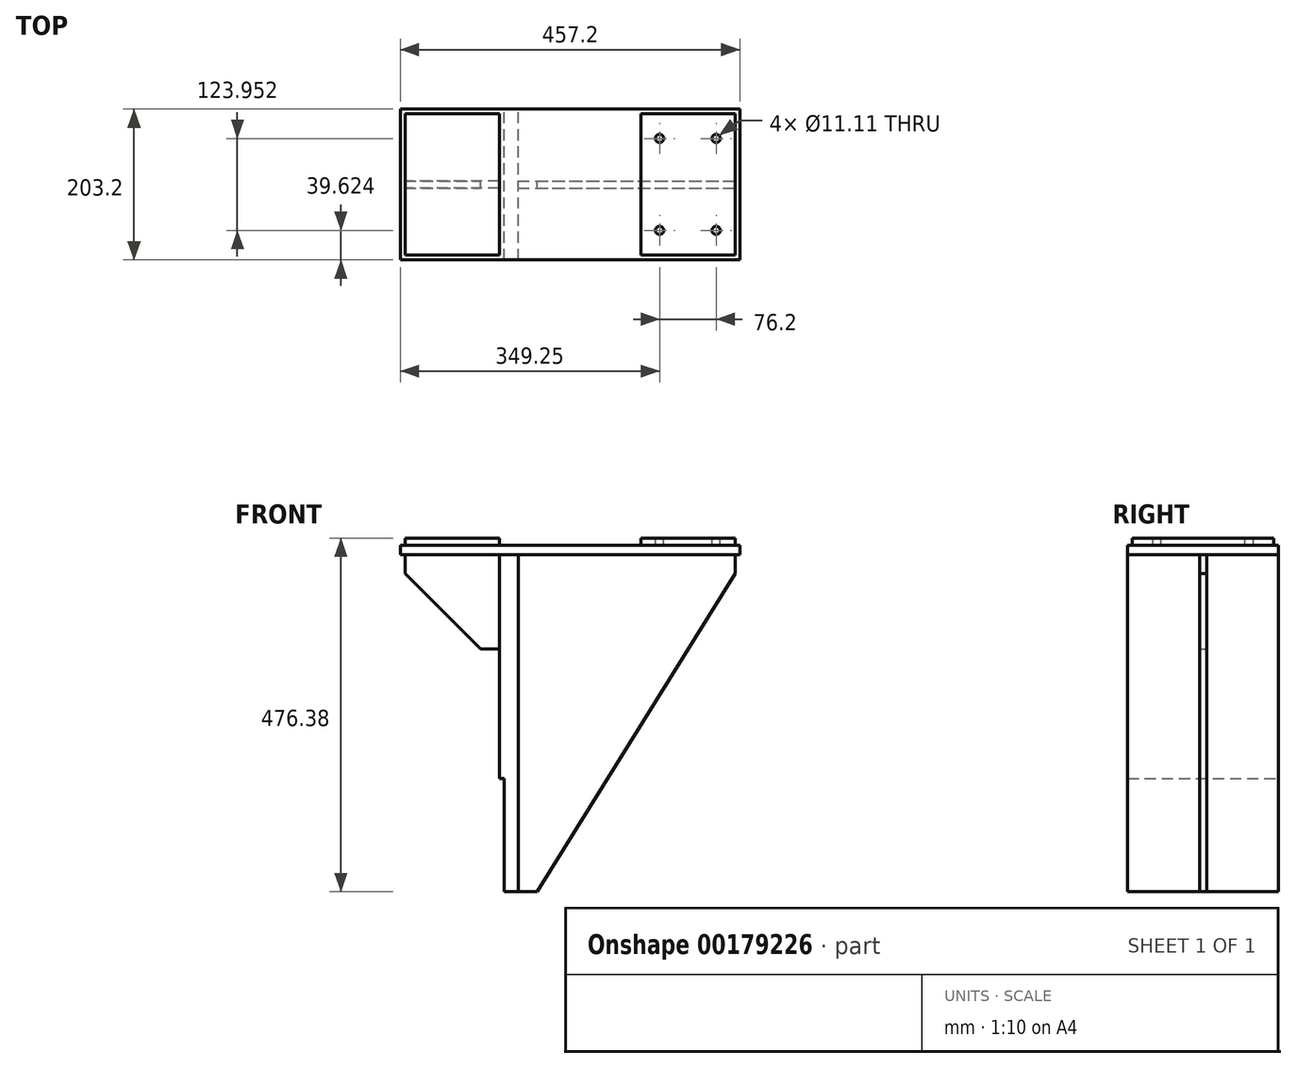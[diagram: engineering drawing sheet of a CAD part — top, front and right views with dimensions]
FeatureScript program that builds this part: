
annotation { "Feature Type Name" : "Feature", "Feature Type Description" : "" }
export const myFeature = defineFeature(function(context is Context, id is Id, definition is map)
    precondition{}
    {
        {
            var Q0;
            Q0=qCreatedBy(makeId("Front.planeOp"),FACE);
            var sketch = newSketch(context, id + "F0", { "sketchPlane" : qUnion([Q0])});
            skLineSegment(sketch, "E0.bottom", {"start": v(0, -454.15) * mm, "end": v(-19.05, -454.15) * mm});
            skLineSegment(sketch, "E0.top", {"start": v(0, 0) * mm, "end": v(-19.05, 0) * mm});
            skLineSegment(sketch, "E0.left", {"start": v(0, -454.15) * mm, "end": v(0, 0) * mm});
            skLineSegment(sketch, "E0.right", {"start": v(-19.05, -454.15) * mm, "end": v(-19.05, 0) * mm});
            skLineSegment(sketch, "E1.bottom", {"start": v(-19.05, -301.75) * mm, "end": v(-25.4, -301.75) * mm});
            skLineSegment(sketch, "E1.top", {"start": v(-19.05, 0) * mm, "end": v(-25.4, 0) * mm});
            skLineSegment(sketch, "E1.left", {"start": v(-19.05, -301.75) * mm, "end": v(-19.05, 0) * mm});
            skLineSegment(sketch, "E1.right", {"start": v(-25.4, -301.75) * mm, "end": v(-25.4, 0) * mm});
            skSolve(sketch);
        }
        {
            var Q0;
            Q0=makeQuery(id+"F0.imprint","IMPRINT",FACE,{"disambiguationData":[TD([[makeQuery(id+"F0.imprint","IMPRINT",EDGE,{"derivedFrom":sQuery(id+"F0.wireOp",EDGE,"E0.bottom")}),-1.0]])]});
            var Q1;
            Q1=makeQuery(id+"F0.imprint","IMPRINT",FACE,{"disambiguationData":[TD([[makeQuery(id+"F0.imprint","IMPRINT",EDGE,{"derivedFrom":sQuery(id+"F0.wireOp",EDGE,"E1.bottom")}),-1.0]])]});
            extrude(context, id + "F1", {"entities" : qUnion([Q0, Q1]), "endBound" : BoundingType.SYMMETRIC, "depth" : 203.2 * mm});
        }
        {
            var Q0;
            Q0=qCreatedBy(makeId("Front.planeOp"),FACE);
            var sketch = newSketch(context, id + "F2", { "sketchPlane" : qUnion([Q0])});
            skLineSegment(sketch, "E2", {"start": v(0, 0) * mm, "end": v(-158.75, 0) * mm});
            skLineSegment(sketch, "E3", {"start": v(-158.75, 0) * mm, "end": v(-158.75, 12.7) * mm});
            skLineSegment(sketch, "E4", {"start": v(-158.75, 12.7) * mm, "end": v(298.45, 12.7) * mm});
            skLineSegment(sketch, "E5", {"start": v(298.45, 12.7) * mm, "end": v(298.45, 0) * mm});
            skLineSegment(sketch, "E6", {"start": v(298.45, 0) * mm, "end": v(0, 0) * mm});
            skSolve(sketch);
        }
        {
            var Q0;
            Q0=makeQuery(id+"F2.imprint","IMPRINT",FACE,{"disambiguationData":[TD([[makeQuery(id+"F2.imprint","IMPRINT",EDGE,{"derivedFrom":sQuery(id+"F2.wireOp",EDGE,"E2")}),-1.0]])]});
            extrude(context, id + "F3", {"entities" : qUnion([Q0]), "endBound" : BoundingType.SYMMETRIC, "depth" : 203.2 * mm});
        }
        {
            var Q0;
            Q0=qCreatedBy(makeId("Front.planeOp"),FACE);
            var sketch = newSketch(context, id + "F4", { "sketchPlane" : qUnion([Q0])});
            skLineSegment(sketch, "E7.0", {"start": v(-25.4, -301.75) * mm, "end": v(-25.4, 0) * mm, "construction": true});
            skLineSegment(sketch, "E8.0", {"start": v(298.45, 0) * mm, "end": v(-158.75, 0) * mm, "construction": true});
            skLineSegment(sketch, "E9.0", {"start": v(0, -454.15) * mm, "end": v(0, 0) * mm, "construction": true});
            skLineSegment(sketch, "E10.bottom", {"start": v(-25.4, 0) * mm, "end": v(-152.4, 0) * mm});
            skLineSegment(sketch, "E10.top", {"start": v(-25.4, -127) * mm, "end": v(-50.8, -127) * mm});
            skLineSegment(sketch, "E10.left", {"start": v(-25.4, 0) * mm, "end": v(-25.4, -127) * mm});
            skLineSegment(sketch, "E10.right", {"start": v(-152.4, 0) * mm, "end": v(-152.4, -25.4) * mm});
            skLineSegment(sketch, "E11", {"start": v(-152.4, -25.4) * mm, "end": v(-50.8, -127) * mm});
            skSolve(sketch);
        }
        {
            var Q0;
            Q0 = qSketchRegion(id + "F4", true);
            extrude(context, id + "F5", {"entities" : qUnion([Q0]), "endBound" : BoundingType.SYMMETRIC, "depth" : 9.52 * mm});
        }
        {
            var Q0;
            Q0=qCreatedBy(makeId("Front.planeOp"),FACE);
            var sketch = newSketch(context, id + "F6", { "sketchPlane" : qUnion([Q0])});
            skLineSegment(sketch, "E12.0", {"start": v(298.45, 0) * mm, "end": v(-158.75, 0) * mm, "construction": true});
            skLineSegment(sketch, "E13.0", {"start": v(0, -454.15) * mm, "end": v(0, 0) * mm, "construction": true});
            skLineSegment(sketch, "E14.bottom", {"start": v(0, 0) * mm, "end": v(292.1, 0) * mm});
            skLineSegment(sketch, "E14.top", {"start": v(0, -454.15) * mm, "end": v(25.4, -454.15) * mm});
            skLineSegment(sketch, "E14.left", {"start": v(0, 0) * mm, "end": v(0, -454.15) * mm});
            skLineSegment(sketch, "E14.right", {"start": v(292.1, 0) * mm, "end": v(292.1, -25.4) * mm});
            skLineSegment(sketch, "E15", {"start": v(25.4, -454.15) * mm, "end": v(292.1, -25.4) * mm});
            skPoint(sketch, "E16.orphan", {"position": v(292.1, -454.15) * mm});
            skSolve(sketch);
        }
        {
            var Q0;
            Q0 = qSketchRegion(id + "F6", true);
            extrude(context, id + "F7", {"entities" : qUnion([Q0]), "endBound" : BoundingType.SYMMETRIC, "depth" : 9.52 * mm});
        }
        {
            var Q0;
            Q0=makeQuery(id+"F3.opExtrude","SWEPT_FACE",FACE,{"disambiguationData":[OSD([sQuery(id+"F2.wireOp",EDGE,"E4")])]});
            var sketch = newSketch(context, id + "F8", { "sketchPlane" : qUnion([Q0])});
            skLineSegment(sketch, "E17.0.0", {"start": v(298.45, 101.6) * mm, "end": v(-158.75, 101.6) * mm, "construction": true});
            skLineSegment(sketch, "E17.0.1", {"start": v(-158.75, 101.6) * mm, "end": v(-158.75, -101.6) * mm, "construction": true});
            skLineSegment(sketch, "E17.0.2", {"start": v(-158.75, -101.6) * mm, "end": v(298.45, -101.6) * mm, "construction": true});
            skLineSegment(sketch, "E17.0.3", {"start": v(298.45, -101.6) * mm, "end": v(298.45, 101.6) * mm, "construction": true});
            skLineSegment(sketch, "E18.0", {"start": v(292.1, 95.25) * mm, "end": v(-152.4, 95.25) * mm, "construction": true});
            skLineSegment(sketch, "E18.1", {"start": v(292.1, -95.25) * mm, "end": v(292.1, 95.25) * mm, "construction": true});
            skLineSegment(sketch, "E18.2", {"start": v(-152.4, -95.25) * mm, "end": v(292.1, -95.25) * mm, "construction": true});
            skLineSegment(sketch, "E18.3", {"start": v(-152.4, 95.25) * mm, "end": v(-152.4, -95.25) * mm, "construction": true});
            skLineSegment(sketch, "E19.bottom", {"start": v(-152.4, 95.25) * mm, "end": v(-25.4, 95.25) * mm});
            skLineSegment(sketch, "E19.top", {"start": v(-152.4, -95.25) * mm, "end": v(-25.4, -95.25) * mm});
            skLineSegment(sketch, "E19.left", {"start": v(-152.4, 95.25) * mm, "end": v(-152.4, -95.25) * mm});
            skLineSegment(sketch, "E19.right", {"start": v(-25.4, 95.25) * mm, "end": v(-25.4, -95.25) * mm});
            skLineSegment(sketch, "E20.bottom", {"start": v(292.1, 95.25) * mm, "end": v(165.1, 95.25) * mm});
            skLineSegment(sketch, "E20.top", {"start": v(292.1, -95.25) * mm, "end": v(165.1, -95.25) * mm});
            skLineSegment(sketch, "E20.left", {"start": v(292.1, 95.25) * mm, "end": v(292.1, -95.25) * mm});
            skLineSegment(sketch, "E20.right", {"start": v(165.1, 95.25) * mm, "end": v(165.1, -95.25) * mm});
            skSolve(sketch);
        }
        {
            var Q0;
            Q0 = qSketchRegion(id + "F8", true);
            extrude(context, id + "F9", {"entities" : qUnion([Q0]), "depth" : 9.52 * mm});
        }
        {
            var Q0;
            Q0=makeQuery(id+"F9.opExtrude","CAP_FACE",FACE,{"disambiguationData":[OSD([sQuery(id+"F8.wireOp",EDGE,"E20.bottom"),sQuery(id+"F8.wireOp",EDGE,"E20.top"),sQuery(id+"F8.wireOp",EDGE,"E20.left"),sQuery(id+"F8.wireOp",EDGE,"E20.right")])],"isStart":false});
            var sketch = newSketch(context, id + "F10", { "sketchPlane" : qUnion([Q0])});
            skLineSegment(sketch, "E21", {"start": v(329.33, 0) * mm, "end": v(-204.73, 0) * mm, "construction": true});
            skLineSegment(sketch, "E22", {"start": v(228.6, -95.25) * mm, "end": v(228.6, 160.12) * mm, "construction": true});
            skLineSegment(sketch, "E23.0", {"start": v(-152.4, -95.25) * mm, "end": v(-25.4, -95.25) * mm, "construction": true});
            skLineSegment(sketch, "E24", {"start": v(-88.9, -95.25) * mm, "end": v(-88.9, 163.93) * mm, "construction": true});
            skLineSegment(sketch, "E25.0", {"start": v(266.7, -95.25) * mm, "end": v(266.7, 160.12) * mm, "construction": true});
            skLineSegment(sketch, "E26.0", {"start": v(329.33, -61.98) * mm, "end": v(-204.73, -61.98) * mm, "construction": true});
            skLineSegment(sketch, "E27.0", {"start": v(-127, -95.25) * mm, "end": v(-127, 163.93) * mm, "construction": true});
            skPoint(sketch, "E28", {"position": v(266.7, -61.98) * mm});
            skPoint(sketch, "E29.MirrorP", {"position": v(190.5, -61.98) * mm});
            skPoint(sketch, "E30.MirrorP", {"position": v(266.7, 61.98) * mm});
            skPoint(sketch, "E31.MirrorP", {"position": v(190.5, 61.98) * mm});
            skPoint(sketch, "E32", {"position": v(-127, -61.98) * mm});
            skPoint(sketch, "E33.MirrorP", {"position": v(-50.8, -61.98) * mm});
            skPoint(sketch, "E34.MirrorP", {"position": v(-127, 61.98) * mm});
            skPoint(sketch, "E35.MirrorP", {"position": v(-50.8, 61.98) * mm});
            skSolve(sketch);
        }
        {
            var Q0;
            Q0=sQuery(id+"F10.wireOp",VERTEX,"E34.MirrorP");
            var Q1;
            Q1=sQuery(id+"F10.wireOp",VERTEX,"E35.MirrorP");
            var Q2;
            Q2=sQuery(id+"F10.wireOp",VERTEX,"E32");
            var Q3;
            Q3=sQuery(id+"F10.wireOp",VERTEX,"E33.MirrorP");
            var Q4;
            Q4=sQuery(id+"F10.wireOp",VERTEX,"E31.MirrorP");
            var Q5;
            Q5=sQuery(id+"F10.wireOp",VERTEX,"E30.MirrorP");
            var Q6;
            Q6=sQuery(id+"F10.wireOp",VERTEX,"E28");
            var Q7;
            Q7=sQuery(id+"F10.wireOp",VERTEX,"E29.MirrorP");
            var Q8;
            Q8=makeQuery(id+"F9.opExtrude","SWEPT_BODY",BODY,{"disambiguationData":[OSD([sQuery(id+"F8.wireOp",EDGE,"E20.bottom"),sQuery(id+"F8.wireOp",EDGE,"E20.top"),sQuery(id+"F8.wireOp",EDGE,"E20.left"),sQuery(id+"F8.wireOp",EDGE,"E20.right")])]});
            hole(context, id + "F11", {"style" : HoleStyle.SIMPLE, "endStyle" : HoleEndStyle.THROUGH, "standardTappedOrClearance" : lookupTablePath({ "standard" : "ANSI", "size" : "7/16 (0.44)", "type" : "Drilled" }), "standardBlindInLast" : lookupTablePath({ "standard" : "ANSI", "size" : "7/16", "type" : "Drilled" }), "holeDiameter" : 11.1 * mm, "locations" : qUnion([Q0, Q1, Q2, Q3, Q4, Q5, Q6, Q7]), "scope" : qUnion([Q8]), "isTappedThrough" : true});
        }
    });
